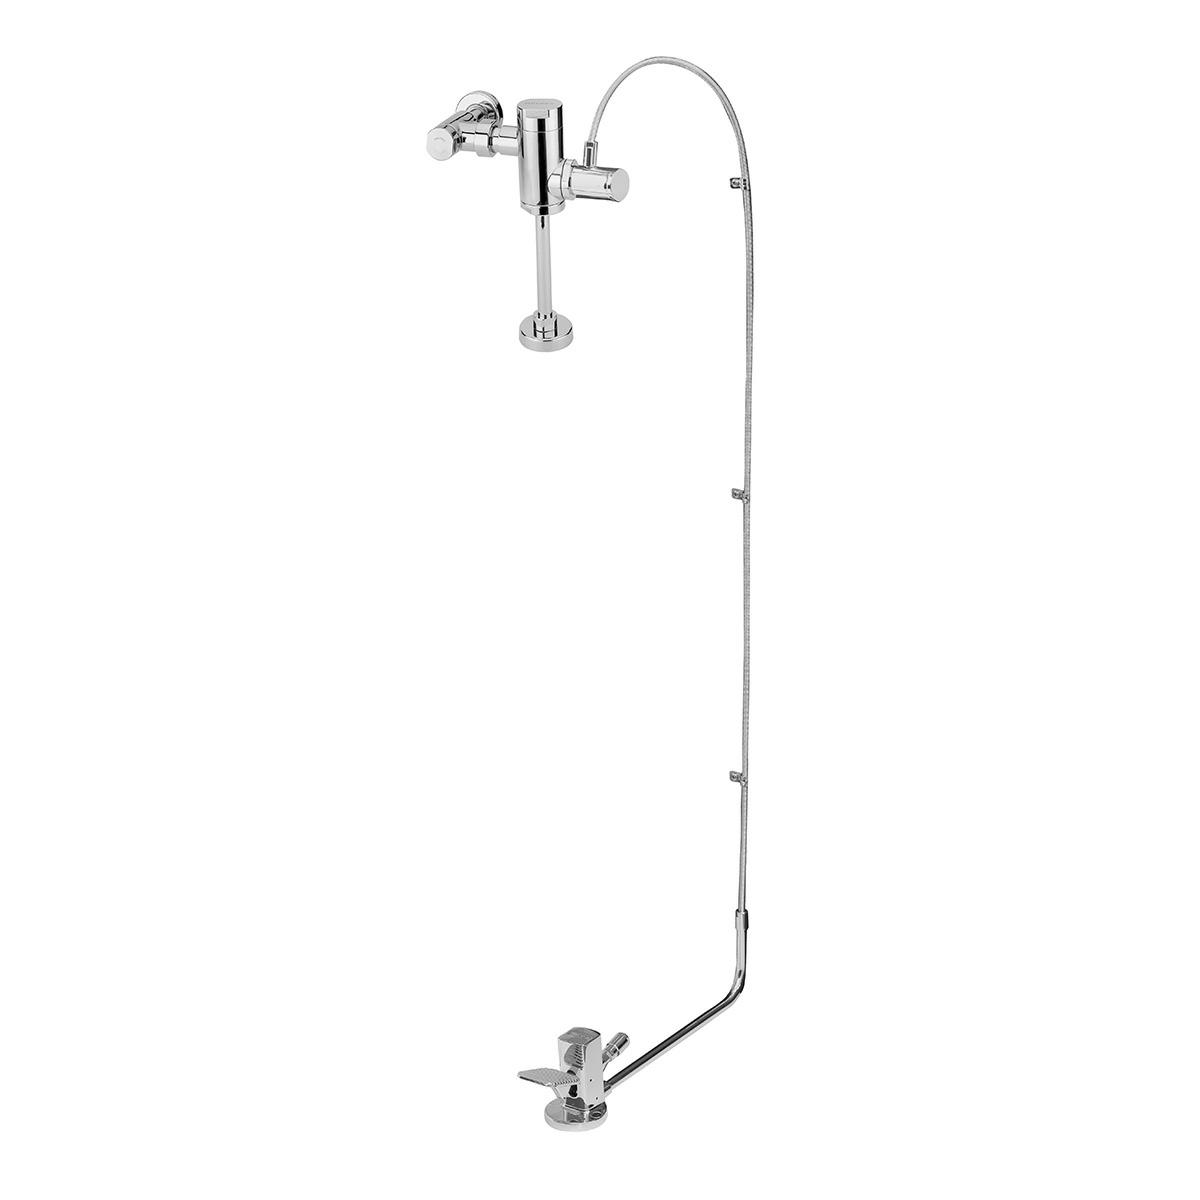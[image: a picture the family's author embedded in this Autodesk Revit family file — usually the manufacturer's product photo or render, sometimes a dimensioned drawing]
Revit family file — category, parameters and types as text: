
# Revit family: 313-19-0.5
name_source: partatom
category: Aparatos sanitarios
units: mm (PartAtom-declared; Revit-internal decimal feet)

## family parameters
Compartido = Sí
Corte con vacíos al cargar = No
Cota de conector redondo = Diámetro de uso
Número OmniClass = 23.45.00.00
Punto de cálculo de habitación = No
Se basa en plano de trabajo = No
Siempre vertical = Sí
Tipo de pieza = Normal
Título OmniClass = Sanitary, Laundry, and Cleaning Equipment

## types (1)
- 185-19
    Chrome = Brass Chromed
    Comentarios de tipo = Flush Valves
    Conexión AF = Sí
    Connection = Conexión de alimentación: tubo 25,4 mm
    Descripción = Fluxómetro de pedal expuesto para mingitorio 0.5LPD
    Documentation = https://www.helvex.com.mx
    Elevación por defecto = 0"
    Fabricante = HELVEX
    Flow = 0,5 L por accionamiento
    Imagen de tipo = 313-19-0.5.jpg
    Instructive = https://www.helvex.com.mx
    Max. Working Pressure = 85.3 psi
    Min. Working Pressure = 14.2 psi
    Modelo = 313-19-0.5
    URL = https://www.helvex.com.mx

## geometry (parser evidence)
native form markers: Sweep x3
no freeform markers — native parametric forms only
